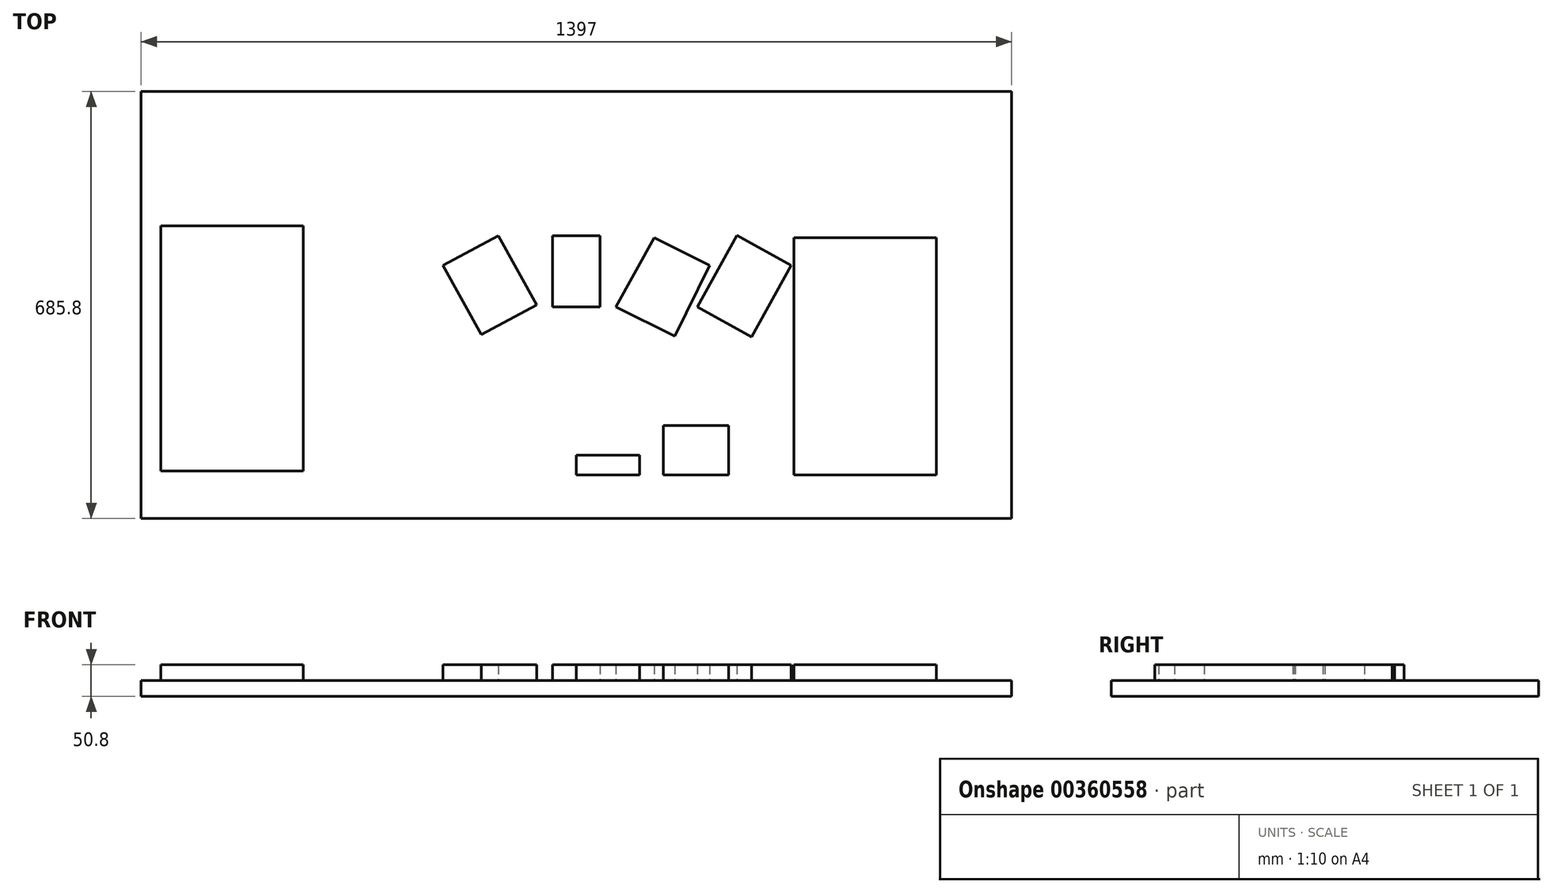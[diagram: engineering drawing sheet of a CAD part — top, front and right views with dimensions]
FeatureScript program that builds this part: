
annotation { "Feature Type Name" : "Feature", "Feature Type Description" : "" }
export const myFeature = defineFeature(function(context is Context, id is Id, definition is map)
    precondition{}
    {
        {
            var Q0;
            Q0=qCreatedBy(makeId("Top.planeOp"),FACE);
            var sketch = newSketch(context, id + "F0", { "sketchPlane" : qUnion([Q0])});
            skLineSegment(sketch, "E0.bottom", {"start": v(698.5, 342.9) * mm, "end": v(-698.5, 342.9) * mm});
            skLineSegment(sketch, "E0.top", {"start": v(698.5, -342.9) * mm, "end": v(-698.5, -342.9) * mm});
            skLineSegment(sketch, "E0.left", {"start": v(698.5, 342.9) * mm, "end": v(698.5, -342.9) * mm});
            skLineSegment(sketch, "E0.right", {"start": v(-698.5, 342.9) * mm, "end": v(-698.5, -342.9) * mm});
            skPoint(sketch, "E0.middle", {"position": v(0, 0) * mm});
            skSolve(sketch);
        }
        {
            var Q0;
            Q0 = qSketchRegion(id + "F0", true);
            extrude(context, id + "F1", {"entities" : qUnion([Q0]), "depth" : 25.4 * mm});
        }
        {
            var Q0;
            Q0=makeQuery(id+"F1.opExtrude","CAP_FACE",FACE,{"disambiguationData":[OSD([sQuery(id+"F0.wireOp",EDGE,"E0.bottom"),sQuery(id+"F0.wireOp",EDGE,"E0.top"),sQuery(id+"F0.wireOp",EDGE,"E0.left"),sQuery(id+"F0.wireOp",EDGE,"E0.right")])],"isStart":false});
            var sketch = newSketch(context, id + "F2", { "sketchPlane" : qUnion([Q0])});
            skLineSegment(sketch, "E1.bottom", {"start": v(241.3, -143.2) * mm, "end": v(-393.7, -143.2) * mm, "construction": true});
            skLineSegment(sketch, "E1.top", {"start": v(241.3, -67) * mm, "end": v(-393.7, -67) * mm, "construction": true});
            skLineSegment(sketch, "E1.left", {"start": v(241.3, -143.2) * mm, "end": v(241.3, -67) * mm, "construction": true});
            skLineSegment(sketch, "E1.right", {"start": v(-393.7, -143.2) * mm, "end": v(-393.7, -67) * mm, "construction": true});
            skPoint(sketch, "E1.middle", {"position": v(-76.2, -105.1) * mm});
            skLineSegment(sketch, "E2.bottom", {"start": v(-38.1, -3.42) * mm, "end": v(38.1, -3.56) * mm});
            skLineSegment(sketch, "E2.left", {"start": v(-38.1, -3.42) * mm, "end": v(-38.1, 110.74) * mm});
            skLineSegment(sketch, "E2.right", {"start": v(38.1, -3.56) * mm, "end": v(38.1, 110.74) * mm});
            skLineSegment(sketch, "E3", {"start": v(38.1, 110.74) * mm, "end": v(-38.1, 110.74) * mm});
            skPoint(sketch, "E4", {"position": v(-3.46, -67) * mm});
            skPoint(sketch, "E5.positionSnap0", {"position": v(241.3, -105.1) * mm});
            skLineSegment(sketch, "E6", {"start": v(-38.1, 110.74) * mm, "end": v(38.1, -3.56) * mm});
            skLineSegment(sketch, "E7", {"start": v(-38.1, -3.42) * mm, "end": v(38.1, 110.74) * mm});
            skPoint(sketch, "E8", {"position": v(-438.15, 127) * mm});
            skLineSegment(sketch, "E9.bottom", {"start": v(-438.15, 127) * mm, "end": v(-666.75, 127) * mm});
            skLineSegment(sketch, "E9.top", {"start": v(-438.15, -266.7) * mm, "end": v(-666.75, -266.7) * mm});
            skLineSegment(sketch, "E9.left", {"start": v(-438.15, 127) * mm, "end": v(-438.15, -266.7) * mm});
            skLineSegment(sketch, "E9.right", {"start": v(-666.75, 127) * mm, "end": v(-666.75, -266.7) * mm});
            skLineSegment(sketch, "E10.bottom", {"start": v(349.25, 107.95) * mm, "end": v(577.85, 107.95) * mm});
            skLineSegment(sketch, "E10.top", {"start": v(349.25, -273.05) * mm, "end": v(577.85, -273.05) * mm});
            skLineSegment(sketch, "E10.left", {"start": v(349.25, 107.95) * mm, "end": v(349.25, -273.05) * mm});
            skLineSegment(sketch, "E10.right", {"start": v(577.85, 107.95) * mm, "end": v(577.85, -273.05) * mm});
            skLineSegment(sketch, "E11.bottom", {"start": v(0, -273.05) * mm, "end": v(101.6, -273.05) * mm});
            skLineSegment(sketch, "E11.top", {"start": v(0, -241.3) * mm, "end": v(101.6, -241.3) * mm});
            skLineSegment(sketch, "E11.left", {"start": v(0, -273.05) * mm, "end": v(0, -241.3) * mm});
            skLineSegment(sketch, "E11.right", {"start": v(101.6, -273.05) * mm, "end": v(101.6, -241.3) * mm});
            skLineSegment(sketch, "E12", {"start": v(0, -273.05) * mm, "end": v(101.6, -241.3) * mm});
            skLineSegment(sketch, "E13.top", {"start": v(139.7, -193.64) * mm, "end": v(244.2, -193.64) * mm});
            skLineSegment(sketch, "E13.left", {"start": v(139.7, -273.05) * mm, "end": v(139.7, -193.64) * mm});
            skLineSegment(sketch, "E13.right", {"start": v(244.2, -273.05) * mm, "end": v(244.2, -193.64) * mm});
            skLineSegment(sketch, "E14", {"start": v(139.7, -273.05) * mm, "end": v(244.2, -273.05) * mm});
            skLineSegment(sketch, "E15", {"start": v(63.5, -3.56) * mm, "end": v(157.79, -50.21) * mm});
            skLineSegment(sketch, "E16", {"start": v(157.79, -50.21) * mm, "end": v(214.04, 63.5) * mm});
            skLineSegment(sketch, "E17", {"start": v(214.04, 63.5) * mm, "end": v(124.98, 107.56) * mm});
            skLineSegment(sketch, "E18", {"start": v(124.98, 107.56) * mm, "end": v(63.5, -3.56) * mm});
            skLineSegment(sketch, "E19", {"start": v(194.13, -3.56) * mm, "end": v(280.86, -51.55) * mm});
            skLineSegment(sketch, "E20", {"start": v(280.86, -51.55) * mm, "end": v(344.51, 63.5) * mm});
            skLineSegment(sketch, "E21", {"start": v(344.51, 63.5) * mm, "end": v(257.78, 111.49) * mm});
            skLineSegment(sketch, "E22", {"start": v(257.78, 111.49) * mm, "end": v(194.13, -3.56) * mm});
            skPoint(sketch, "E23.endSnap0", {"position": v(0, 342.9) * mm});
            skLineSegment(sketch, "E24.MirrorCS", {"start": v(-124.98, 111.13) * mm, "end": v(-63.5, 0) * mm});
            skLineSegment(sketch, "E25.MirrorCS", {"start": v(-213.88, 63.5) * mm, "end": v(-124.98, 111.13) * mm});
            skLineSegment(sketch, "E26.MirrorCS", {"start": v(-63.5, 0) * mm, "end": v(-152.4, -47.63) * mm});
            skLineSegment(sketch, "E27.MirrorCS", {"start": v(-152.4, -47.63) * mm, "end": v(-213.88, 63.5) * mm});
            skLineSegment(sketch, "E28.MirrorCS", {"start": v(-255.61, 111.13) * mm, "end": v(-194.13, 0) * mm});
            skLineSegment(sketch, "E29.MirrorCS", {"start": v(-194.13, 0) * mm, "end": v(-283.03, -49.19) * mm});
            skLineSegment(sketch, "E30.MirrorCS", {"start": v(-283.03, -49.19) * mm, "end": v(-344.51, 63.5) * mm});
            skLineSegment(sketch, "E31.MirrorCS", {"start": v(-344.51, 63.5) * mm, "end": v(-255.61, 112.69) * mm});
            skPoint(sketch, "E32", {"position": v(110.64, -26.89) * mm});
            skPoint(sketch, "E33", {"position": v(-107.95, -23.81) * mm});
            skPoint(sketch, "E34", {"position": v(-238.58, -24.6) * mm});
            skPoint(sketch, "E35", {"position": v(237.5, -27.55) * mm});
            skPoint(sketch, "E36", {"position": v(-438.15, -69.85) * mm});
            skPoint(sketch, "E37", {"position": v(349.25, -82.55) * mm});
            skPoint(sketch, "E38", {"position": v(38.1, -257.18) * mm});
            skPoint(sketch, "E38.positionSnap0", {"position": v(50.8, -257.18) * mm});
            skPoint(sketch, "E39", {"position": v(191.95, -233.35) * mm});
            skPoint(sketch, "E39.positionSnap0", {"position": v(191.95, -193.64) * mm});
            skPoint(sketch, "E39.positionSnap1", {"position": v(139.7, -233.35) * mm});
            skSolve(sketch);
        }
        {
            var Q0;
            Q0 = qSketchRegion(id + "F2", true);
            extrude(context, id + "F3", {"entities" : qUnion([Q0]), "depth" : 25.4 * mm});
        }
    });
